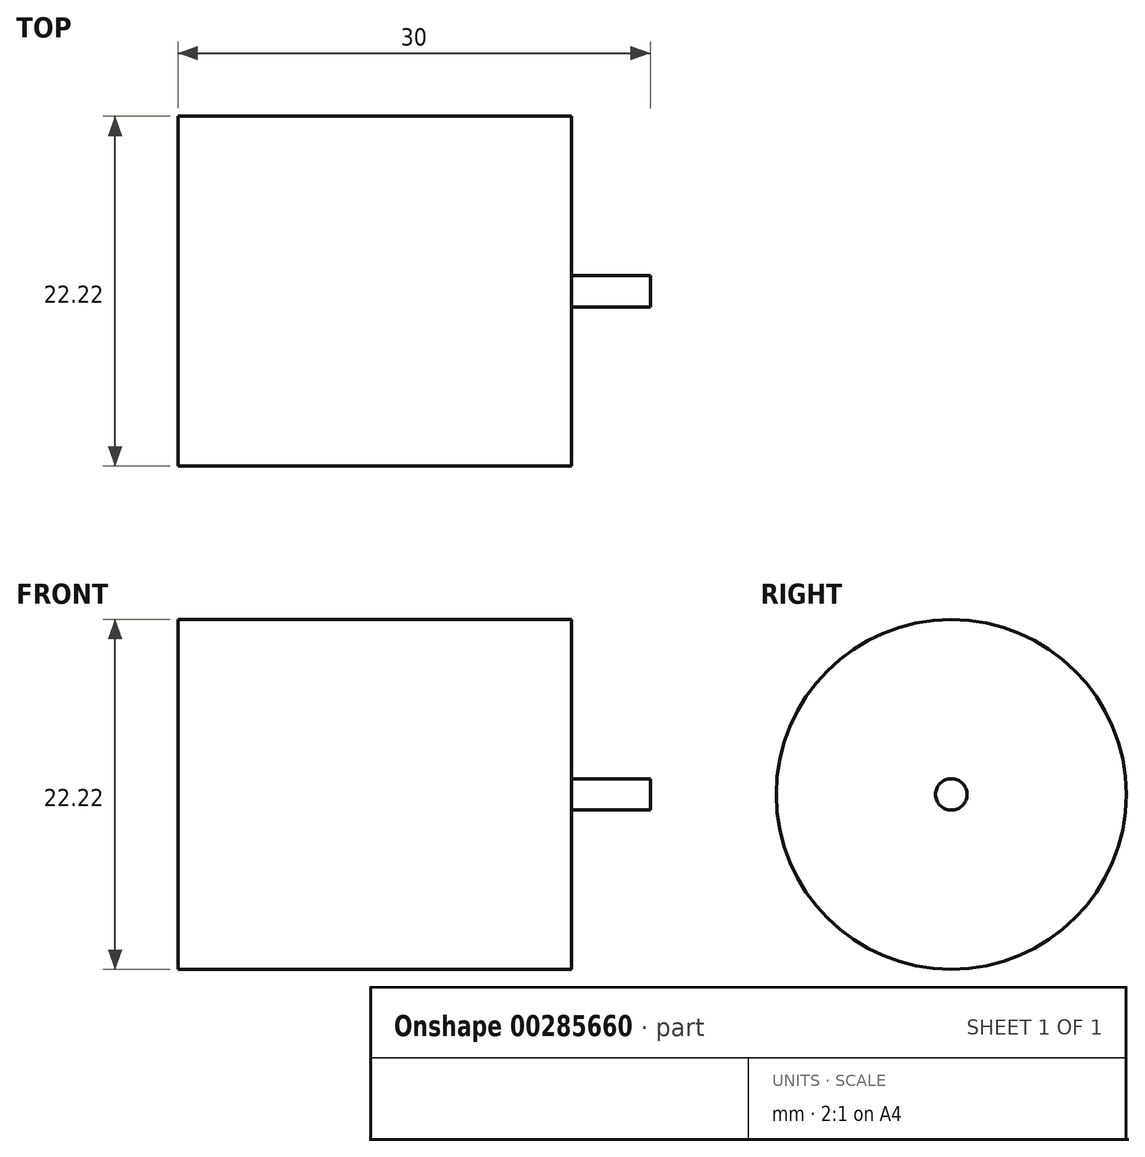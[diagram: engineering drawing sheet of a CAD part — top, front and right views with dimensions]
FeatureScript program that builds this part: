
annotation { "Feature Type Name" : "Feature", "Feature Type Description" : "" }
export const myFeature = defineFeature(function(context is Context, id is Id, definition is map)
    precondition{}
    {
        {
            var Q0;
            Q0=qCreatedBy(makeId("Top.planeOp"),FACE);
            var sketch = newSketch(context, id + "F0", { "sketchPlane" : qUnion([Q0])});
            skLineSegment(sketch, "E0.bottom", {"start": v(0, 0) * mm, "end": v(-25, 0) * mm});
            skLineSegment(sketch, "E0.top", {"start": v(0, 11.11) * mm, "end": v(-25, 11.11) * mm});
            skLineSegment(sketch, "E0.left", {"start": v(0, 0) * mm, "end": v(0, 11.11) * mm});
            skLineSegment(sketch, "E0.right", {"start": v(-25, 0) * mm, "end": v(-25, 11.11) * mm});
            skSolve(sketch);
        }
        {
            var Q0;
            Q0=makeQuery(id+"F0.imprint","IMPRINT",FACE,{"disambiguationData":[TD([[makeQuery(id+"F0.imprint","IMPRINT",EDGE,{"derivedFrom":sQuery(id+"F0.wireOp",EDGE,"E0.bottom")}),-1.0]])]});
            var Q1;
            Q1=sQuery(id+"F0.wireOp",EDGE,"E0.bottom");
            revolve(context, id + "F1", {"entities" : qUnion([Q0]), "axis" : qUnion([Q1]), "revolveType" : RevolveType.FULL});
        }
        {
            var Q0;
            Q0=makeQuery(id+"F1.opRevolve","SWEPT_FACE",FACE,{"disambiguationData":[OSD([sQuery(id+"F0.wireOp",EDGE,"E0.left")])]});
            var sketch = newSketch(context, id + "F2", { "sketchPlane" : qUnion([Q0])});
            skCircle(sketch, "E1", {"center": v(0, 0) * mm, "radius": 1 * mm});
            skSolve(sketch);
        }
        {
            var Q0;
            Q0=makeQuery(id+"F2.imprint","IMPRINT",FACE,{"disambiguationData":[TD([[makeQuery(id+"F2.imprint","IMPRINT",EDGE,{"derivedFrom":sQuery(id+"F2.wireOp",EDGE,"E1")}),1.0]])]});
            extrude(context, id + "F3", {"entities" : qUnion([Q0]), "operationType" : NewBodyOperationType.ADD, "depth" : 5 * mm});
        }
    });
